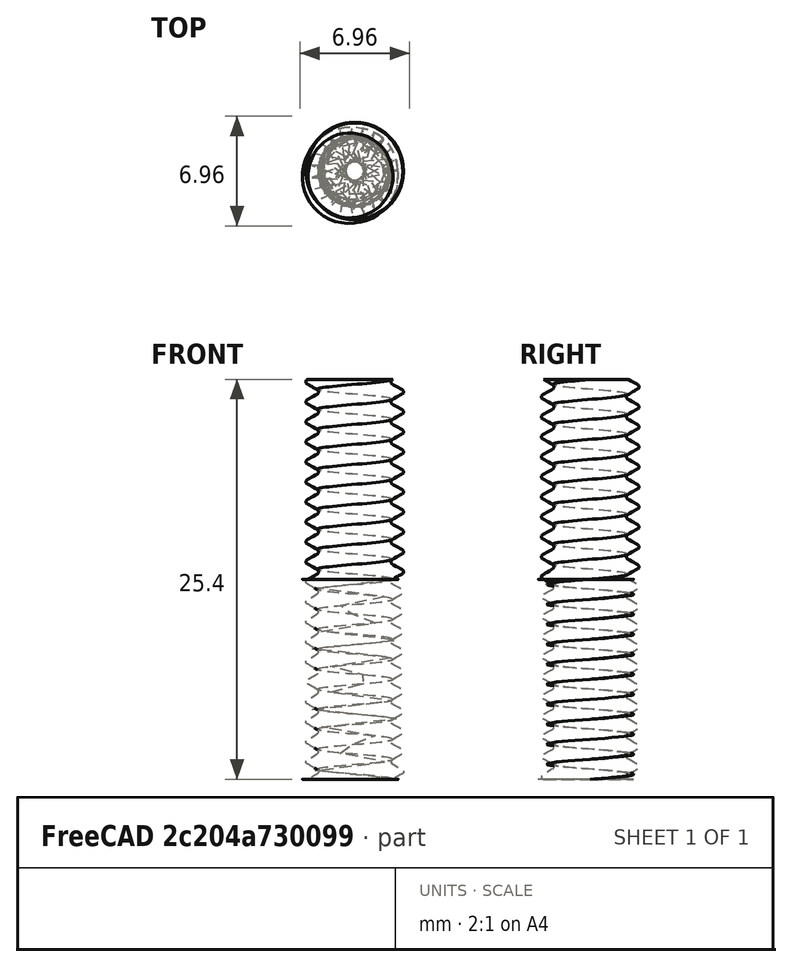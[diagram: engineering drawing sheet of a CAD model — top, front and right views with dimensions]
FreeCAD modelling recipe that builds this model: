
FCSTD DOCUMENT  (FreeCAD 2023.810R14555 (Git shallow))
Label: 1_4 screws
License: All rights reserved
LicenseURL: https://en.wikipedia.org/wiki/All_rights_reserved
objects: Part::Part2DObjectPython×2, Part::Helix×2, Part::Sweep×2
note: 6 computed .brp shape members not serialized (recipe doc carries the construction recipe); baked Part::Feature solids carry a one-line shape summary decoded from their .brp

FEATURE [Part::Part2DObjectPython] VThreadProfile  # Draft 2D object (typed FeaturePython)
  Area = 22.828
  Closed = true
  Continuity = C3
  FixShape = 1
  Instructions = Expand this with the ... button to view instructions | Sweep this object along a helix of the same pitch to produce your thread. | It is recommended to make the helix in the ThreadProfile workbench. | If there is an active Body the ThreadProfile object will be put into it.,If not it can be dragged and dropped into the body later. | If there is an active Body when the helix is made there will be made a ShapeBinder for it | For internal threads you will need to cut the Sweep object out of a cylinder, or if using Part Design sweep it as a Subtractive Pipe. | Always use Frenet mode | I have provided some presets, but it is possible there could be some errors.  Double check for mission critical applications. | Also, the tolerances might be different from what you wish to have.  I believe the internal minor diameters are all minimum and the external are all maximum.
  InternalOrExternal = 1
  InvalidShape = false
  MakeFace = true
  MinorDiameter = 4.79298
  Parameterization = 1
  Pitch = 1.27
  Points = (719) [(2.39341,0.020916,0),(2.39027,0.0417803,0),(2.38706,0.0625944,0),(2.38378,0.0833591,0),(2.38041,0.104075,0),(2.37694,0.124744,0),(2.37339,0.145365,0),+712 more]
  Presets = 213
  Quality = 1
  ThreadCount = 20
  TreeRank = 5
  ValidateShape = false
  Version = 1.69
  external_data = [-0.00235387,-0.00461052,-0.00677828,-0.00886428,-0.0108747,-0.0128149,-0.0146895,-0.0165028,-0.0182584,-0.0199597,-0.0216095,-0.0232106,-0.0247653,-0.0262759,-0.0277444,-0.0291725,-0.0305621,-0.0319145,-0.0332313,-0.0345138,-0.0357632,+698 more]
  internal_data = [0,0,0,0,0,0,0,0,0,0,0,0,0,0,0,0,0,0,0,0,0,0,0,0,0,0,0,0,0,0,0,0,0,0,0,0,0,0,0,0,0,0,0,0,0,0,0,0,0,0,0,0,0,0,0,0,0,0,0,0,0,0,0,0,0,0,0,0,0,0,0,0,0,0,0,0,0,0,0,0,0,0,0,0,0,0,0,0,0,0,0,0,0,0,0,0,0,0,0,0,0,0,0,0,0,0,0,0,0,0,0,0,0,0,0,0,0,0,0,0,+599 more]
  preset_names = <blob: 3959 chars omitted>
  presets_data = [0,0,0,2.20878,24.1173,24.6888,0.25,0.693,0.729,0.25,0.793,0.829,0.25,0.893,0.929,0.3,1.032,1.075,0.35,1.171,1.221,0.35,1.371,1.421,0.4,1.509,1.567,0.45,1.648,1.713,0.45,1.948,2.013,0.5,2.387,2.459,0.6,2.764,2.85,0.7,3.141,3.242,0.75,3.58,+712 more]
FEATURE [Part::Helix] Helix
  Angle = 0
  AttacherType = Attacher::AttachEngine3D
  FixShape = 1
  Height = 25.4
  InvalidShape = false
  LocalCoord = 0
  Pitch = 1.27
  Radius = 1
  SegmentLength = 0
  Style = 0
  TreeRank = 6
  ValidateShape = false
  expr: Placement.Base.x = VThreadProfile.Placement.Base.x
  expr: Placement.Base.y = VThreadProfile.Placement.Base.y
  expr: Placement.Base.z = VThreadProfile.Placement.Base.z
  expr: Placement.Rotation.Angle = VThreadProfile.Placement.Rotation.Angle
  expr: Placement.Rotation.Axis.x = VThreadProfile.Placement.Rotation.Axis.x
  expr: Placement.Rotation.Axis.y = VThreadProfile.Placement.Rotation.Axis.y
  expr: Placement.Rotation.Axis.z = VThreadProfile.Placement.Rotation.Axis.z
  expr: Height = VThreadProfile.ThreadCount * VThreadProfile.Pitch
  expr: Pitch = VThreadProfile.Pitch
FEATURE [Part::Sweep] Sweep  label="20 threads"
  FixShape = 1
  Frenet = true
  InvalidShape = false
  Linearize = true
  Sections = -> [VThreadProfile]
  Solid = true
  Spine = -> Helix [Edge1]
  Transition = 1
  TreeRank = 7
  ValidateShape = false
FEATURE [Part::Part2DObjectPython] VThreadProfile001  # Draft 2D object (typed FeaturePython)
  Area = 29.5484
  Closed = true
  Continuity = C3
  FixShape = 1
  Instructions = Expand this with the ... button to view instructions | Sweep this object along a helix of the same pitch to produce your thread. | It is recommended to make the helix in the ThreadProfile workbench. | If there is an active Body the ThreadProfile object will be put into it.,If not it can be dragged and dropped into the body later. | If there is an active Body when the helix is made there will be made a ShapeBinder for it | For internal threads you will need to cut the Sweep object out of a cylinder, or if using Part Design sweep it as a Subtractive Pipe. | Always use Frenet mode | I have provided some presets, but it is possible there could be some errors.  Double check for mission critical applications. | Also, the tolerances might be different from what you wish to have.  I believe the internal minor diameters are all minimum and the external are all maximum.
  InternalOrExternal = 0
  InvalidShape = false
  MakeFace = true
  MinorDiameter = 5.5
  Parameterization = 1
  Pitch = 1.27
  Points = (719) [(2.74989,0.0240313,0),(2.74958,0.0480609,0),(2.74906,0.0720867,0),(2.74832,0.096107,0),(2.74738,0.12012,0),(2.74622,0.144124,0),(2.74486,0.168117,0),+712 more]
  Presets = 213
  Quality = 1
  ThreadCount = 10
  TreeRank = 12
  ValidateShape = false
  Version = 1.69
  external_data = [-0.00235387,-0.00461052,-0.00677828,-0.00886428,-0.0108747,-0.0128149,-0.0146895,-0.0165028,-0.0182584,-0.0199597,-0.0216095,-0.0232106,-0.0247653,-0.0262759,-0.0277444,-0.0291725,-0.0305621,-0.0319145,-0.0332313,-0.0345138,-0.0357632,+698 more]
  internal_data = [0,0,0,0,0,0,0,0,0,0,0,0,0,0,0,0,0,0,0,0,0,0,0,0,0,0,0,0,0,0,0,0,0,0,0,0,0,0,0,0,0,0,0,0,0,0,0,0,0,0,0,0,0,0,0,0,0,0,0,0,0,0,0,0,0,0,0,0,0,0,0,0,0,0,0,0,0,0,0,0,0,0,0,0,0,0,0,0,0,0,0,0,0,0,0,0,0,0,0,0,0,0,0,0,0,0,0,0,0,0,0,0,0,0,0,0,0,0,0,0,+599 more]
  preset_names = <blob: 3959 chars omitted>
  presets_data = [0,0,0,2.20878,24.1173,24.6888,0.25,0.693,0.729,0.25,0.793,0.829,0.25,0.893,0.929,0.3,1.032,1.075,0.35,1.171,1.221,0.35,1.371,1.421,0.4,1.509,1.567,0.45,1.648,1.713,0.45,1.948,2.013,0.5,2.387,2.459,0.6,2.764,2.85,0.7,3.141,3.242,0.75,3.58,+712 more]
FEATURE [Part::Helix] Helix001
  Angle = 0
  AttacherType = Attacher::AttachEngine3D
  FixShape = 1
  Height = 12.7
  InvalidShape = false
  LocalCoord = 0
  Pitch = 1.27
  Radius = 1
  SegmentLength = 0
  Style = 0
  TreeRank = 13
  ValidateShape = false
  expr: Placement.Base.x = VThreadProfile001.Placement.Base.x
  expr: Placement.Base.y = VThreadProfile001.Placement.Base.y
  expr: Placement.Base.z = VThreadProfile001.Placement.Base.z
  expr: Placement.Rotation.Angle = VThreadProfile001.Placement.Rotation.Angle
  expr: Placement.Rotation.Axis.x = VThreadProfile001.Placement.Rotation.Axis.x
  expr: Placement.Rotation.Axis.y = VThreadProfile001.Placement.Rotation.Axis.y
  expr: Placement.Rotation.Axis.z = VThreadProfile001.Placement.Rotation.Axis.z
  expr: Height = VThreadProfile001.ThreadCount * VThreadProfile001.Pitch
  expr: Pitch = VThreadProfile001.Pitch
FEATURE [Part::Sweep] Sweep001  label="10 threads internal oversized"
  FixShape = 1
  Frenet = true
  InvalidShape = false
  Linearize = true
  Sections = -> [VThreadProfile001]
  Solid = true
  Spine = -> Helix001 [Edge1]
  Transition = 1
  TreeRank = 14
  ValidateShape = false
